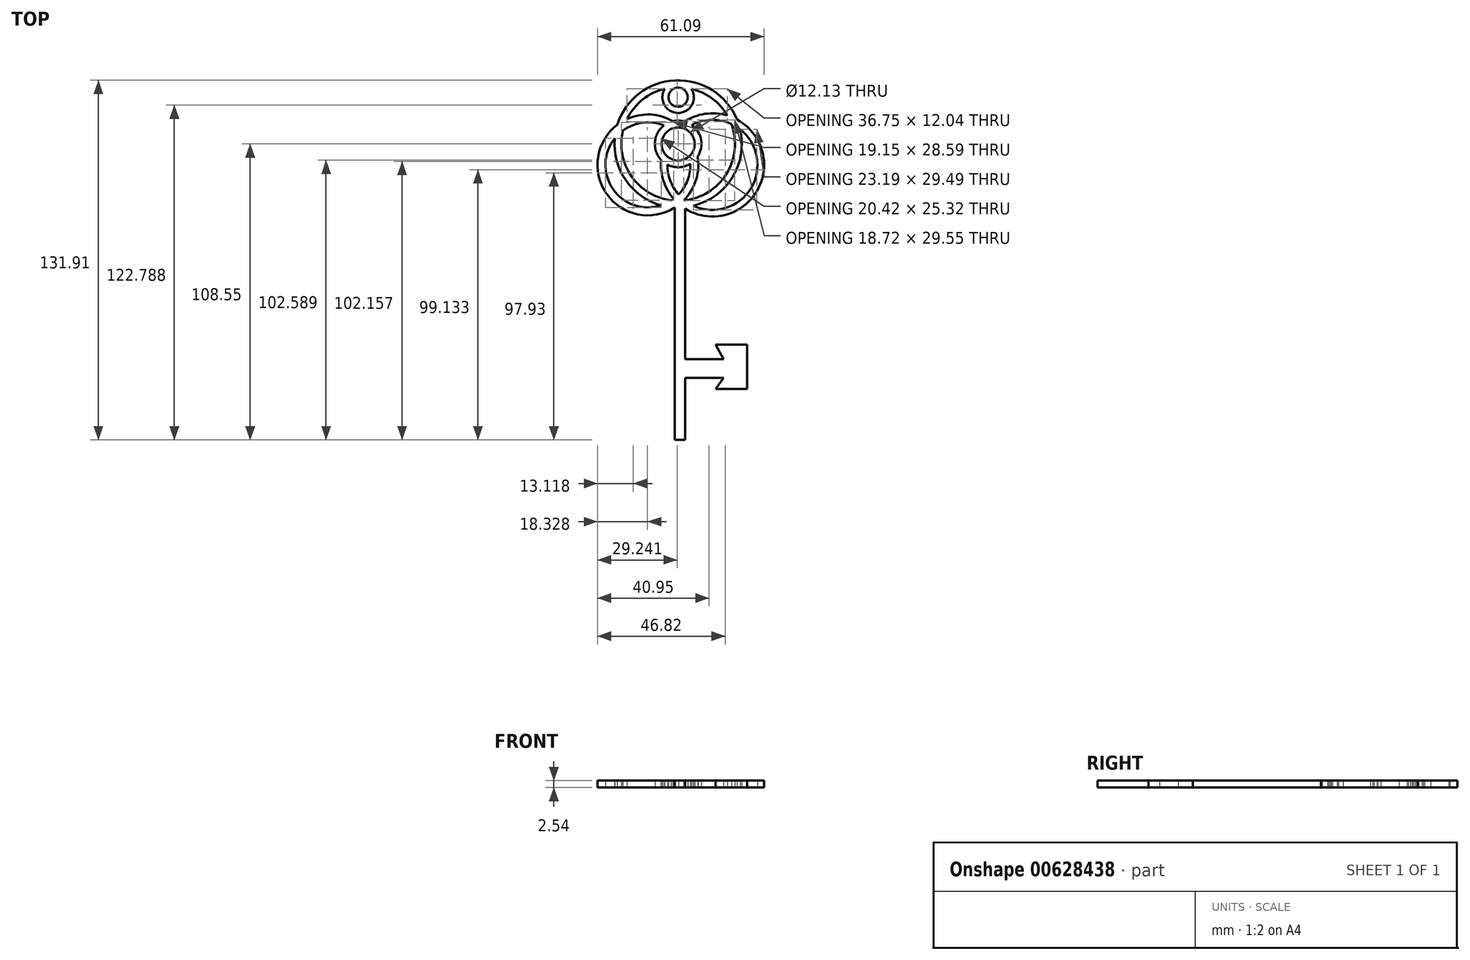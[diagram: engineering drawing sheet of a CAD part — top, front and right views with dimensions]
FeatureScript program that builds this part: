
annotation { "Feature Type Name" : "Feature", "Feature Type Description" : "" }
export const myFeature = defineFeature(function(context is Context, id is Id, definition is map)
    precondition{}
    {
        {
            var Q0;
            Q0=qCreatedBy(makeId("Top.planeOp"),FACE);
            var sketch = newSketch(context, id + "F0", { "sketchPlane" : qUnion([Q0])});
            skArc(sketch, "E0", {"start": v(-4.87, 72.9) * mm, "mid": v(-20.8, 51.43) * mm, "end": v(-2.48, 31.96) * mm});
            skArc(sketch, "E1", {"start": v(-3.92, 45.05) * mm, "mid": v(-2.9, 39.22) * mm, "end": v(0.13, 34.13) * mm});
            skArc(sketch, "E2", {"start": v(-6.24, 46.8) * mm, "mid": v(-5.43, 39.2) * mm, "end": v(-1.68, 32.53) * mm});
            skCircle(sketch, "E3", {"center": v(0, 52.65) * mm, "radius": 23.36 * mm});
            skCircle(sketch, "E4", {"center": v(0, 52.65) * mm, "radius": 6.06 * mm});
            skCircle(sketch, "E5", {"center": v(0, 52.65) * mm, "radius": 8.55 * mm});
            skCircle(sketch, "E6", {"center": v(0, 69.8) * mm, "radius": 3.52 * mm});
            skCircle(sketch, "E7", {"center": v(0, 69.8) * mm, "radius": 5.78 * mm});
            skLineSegment(sketch, "E8", {"start": v(-1.23, 29.32) * mm, "end": v(-1.23, -55.9) * mm});
            skLineSegment(sketch, "E9", {"start": v(-1.23, -55.9) * mm, "end": v(2.51, -55.9) * mm});
            skLineSegment(sketch, "E10", {"start": v(2.51, -55.9) * mm, "end": v(2.51, 28.95) * mm});
            skLineSegment(sketch, "E11", {"start": v(2.51, -21) * mm, "end": v(2.51, -18.04) * mm});
            skLineSegment(sketch, "E12", {"start": v(2.51, -26.32) * mm, "end": v(16.71, -26.32) * mm});
            skLineSegment(sketch, "E13", {"start": v(16.71, -26.32) * mm, "end": v(13.79, -21) * mm});
            skLineSegment(sketch, "E14", {"start": v(13.79, -21) * mm, "end": v(25.29, -21) * mm});
            skLineSegment(sketch, "E15", {"start": v(25.29, -21) * mm, "end": v(25.29, -37.27) * mm});
            skLineSegment(sketch, "E16", {"start": v(25.29, -37.27) * mm, "end": v(13.79, -37.27) * mm});
            skLineSegment(sketch, "E17", {"start": v(13.79, -37.27) * mm, "end": v(16.71, -33.13) * mm});
            skLineSegment(sketch, "E18", {"start": v(16.71, -33.13) * mm, "end": v(2.51, -33.13) * mm});
            skArc(sketch, "E19.trimOffspring", {"start": v(-22.28, 59.68) * mm, "mid": v(-26.29, 34.42) * mm, "end": v(-1.23, 29.32) * mm});
            skArc(sketch, "E20.trimOffspring", {"start": v(-23.27, 54.7) * mm, "mid": v(-23.9, 36.08) * mm, "end": v(-6.25, 30.14) * mm});
            skArc(sketch, "E21.trimOffspring", {"start": v(-1.88, 60.99) * mm, "mid": v(-10.2, 63.43) * mm, "end": v(-18.71, 61.8) * mm});
            skArc(sketch, "E22.trimOffspring", {"start": v(-5.23, 59.4) * mm, "mid": v(-12.97, 60.44) * mm, "end": v(-20.24, 57.58) * mm});
            skArc(sketch, "E23.trimOffspring", {"start": v(2.21, 32.12) * mm, "mid": v(2.31, 32.04) * mm, "end": v(2.42, 31.96) * mm});
            skArc(sketch, "E24.trimOffspring", {"start": v(1.88, 29.36) * mm, "mid": v(28.74, 35.1) * mm, "end": v(21.58, 61.6) * mm});
            skArc(sketch, "E25.trimOffspring", {"start": v(5.65, 29.98) * mm, "mid": v(26.68, 36.35) * mm, "end": v(22.75, 57.98) * mm});
            skArc(sketch, "E26.trimOffspring", {"start": v(-2.48, 31.96) * mm, "mid": v(2.74, 37.77) * mm, "end": v(4.5, 45.38) * mm});
            skArc(sketch, "E27.trimOffspring", {"start": v(19.51, 59.95) * mm, "mid": v(12.2, 61.46) * mm, "end": v(4.97, 59.6) * mm});
            skArc(sketch, "E28.trimOffspring", {"start": v(18.04, 63.08) * mm, "mid": v(9.95, 63.7) * mm, "end": v(2.35, 60.87) * mm});
            skArc(sketch, "E29.trimOffspring", {"start": v(2.01, 31.91) * mm, "mid": v(20.78, 51.2) * mm, "end": v(4.87, 72.9) * mm});
            skLineSegment(sketch, "E30", {"start": v(2.42, 31.96) * mm, "end": v(-2.48, 31.96) * mm});
            skArc(sketch, "E31.trimOffspring", {"start": v(2.01, 31.91) * mm, "mid": v(6.52, 39.32) * mm, "end": v(7.15, 47.97) * mm});
            skSolve(sketch);
        }
        {
            var Q0;
            {var subQ9=sQuery(id+"F0.wireOp",EDGE,"E7");var subQ21=sQuery(id+"F0.wireOp",EDGE,"E0");var subQ24=makeQuery(id+"F0.imprint","INTERSECT",VERTEX,{"derivedFrom":[subQ21,subQ9]});Q0=makeQuery(id+"F0.imprint","IMPRINT",FACE,{"disambiguationData":[TD([[makeQuery(id+"F0.imprint","IMPRINT",EDGE,{"disambiguationData":[TD([[subQ24,-1.0]])],"derivedFrom":subQ21}),-1.0]])]});}
            var Q1;
            Q1=makeQuery(id+"F0.imprint","IMPRINT",FACE,{"disambiguationData":[TD([[makeQuery(id+"F0.imprint","IMPRINT",EDGE,{"derivedFrom":sQuery(id+"F0.wireOp",EDGE,"E6")}),-1.0]])]});
            var Q2;
            {var subQ0=sQuery(id+"F0.wireOp",EDGE,"E27.trimOffspring");Q2=makeQuery(id+"F0.imprint","IMPRINT",FACE,{"disambiguationData":[TD([[makeQuery(id+"F0.imprint","IMPRINT",EDGE,{"derivedFrom":subQ0}),-1.0]])]});}
            var Q3;
            Q3=makeQuery(id+"F0.imprint","IMPRINT",FACE,{"disambiguationData":[TD([[makeQuery(id+"F0.imprint","IMPRINT",EDGE,{"derivedFrom":sQuery(id+"F0.wireOp",EDGE,"E4")}),-1.0]])]});
            var Q4;
            {var subQ0=sQuery(id+"F0.wireOp",EDGE,"E21.trimOffspring");Q4=makeQuery(id+"F0.imprint","IMPRINT",FACE,{"disambiguationData":[TD([[makeQuery(id+"F0.imprint","IMPRINT",EDGE,{"derivedFrom":subQ0}),1.0]])]});}
            var Q5;
            {var subQ0=sQuery(id+"F0.wireOp",EDGE,"E19.trimOffspring");Q5=makeQuery(id+"F0.imprint","IMPRINT",FACE,{"disambiguationData":[TD([[makeQuery(id+"F0.imprint","IMPRINT",EDGE,{"derivedFrom":subQ0}),1.0]])]});}
            var Q6;
            {var subQ0=sQuery(id+"F0.wireOp",EDGE,"E26.trimOffspring");var subQ2=sQuery(id+"F0.wireOp",EDGE,"E5");var subQ3=makeQuery(id+"F0.imprint","INTERSECT",VERTEX,{"derivedFrom":[subQ2,subQ0]});Q6=makeQuery(id+"F0.imprint","IMPRINT",FACE,{"disambiguationData":[TD([[makeQuery(id+"F0.imprint","IMPRINT",EDGE,{"disambiguationData":[TD([[subQ3,-1.0]])],"derivedFrom":subQ2}),-1.0]])]});}
            var Q7;
            {var subQ4=sQuery(id+"F0.wireOp",EDGE,"E25.trimOffspring");Q7=makeQuery(id+"F0.imprint","IMPRINT",FACE,{"disambiguationData":[TD([[makeQuery(id+"F0.imprint","IMPRINT",EDGE,{"derivedFrom":subQ4}),-1.0]])]});}
            var Q8;
            {var subQ0=sQuery(id+"F0.wireOp",EDGE,"E1");Q8=makeQuery(id+"F0.imprint","IMPRINT",FACE,{"disambiguationData":[TD([[makeQuery(id+"F0.imprint","IMPRINT",EDGE,{"derivedFrom":subQ0}),-1.0]])]});}
            var Q9;
            {var subQ4=sQuery(id+"F0.wireOp",EDGE,"E8");Q9=makeQuery(id+"F0.imprint","IMPRINT",FACE,{"disambiguationData":[TD([[makeQuery(id+"F0.imprint","IMPRINT",EDGE,{"derivedFrom":subQ4}),1.0]])]});}
            var Q10;
            {var subQ0=sQuery(id+"F0.wireOp",EDGE,"E12");Q10=makeQuery(id+"F0.imprint","IMPRINT",FACE,{"disambiguationData":[TD([[makeQuery(id+"F0.imprint","IMPRINT",EDGE,{"derivedFrom":subQ0}),-1.0]])]});}
            extrude(context, id + "F1", {"entities" : qUnion([Q0, Q1, Q2, Q3, Q4, Q5, Q6, Q7, Q8, Q9, Q10]), "depth" : 2.54 * mm, "offsetDistance" : 25.4 * mm});
        }
    });
